# Revit family: Shower-Handshower_Kit-KOHLER-Fore_Arc-K-35732T
name_source: partatom
category: Plumbing Fixtures
units: mm (PartAtom-declared; Revit-internal decimal feet)

## family parameters
Cut with Voids When Loaded = No
Host = Face
Maintain Annotation Orientation = No
OmniClass Number = 23.31.17.00
OmniClass Title = Showers
Part Type = Normal
Room Calculation Point = No
Round Connector Dimension = Use Diameter
Shared = No

## types (4) — shared parameters
ADA Compliant = No
Assembly Code = D2010700
CW Connection = Yes
Cold Water Inlet = Cold Water Inlet
Date Modified = 10/06/2025
Default Elevation = 42"
Description = Exposed Bath Shower Faucet
Drain Included = No
Flow Rate = 0 GPM
HW Connection = Yes
Handle Clearance = 3 9/16"
Height = 19 1/2"
Hot Water Inlet = Hot Water Inlet
Length = 4 3/16"
Manufacturer = Kohler Co.
Master Format 2014 = 22 42 23
Master Format 2014 Name = Residential Showers
Material = Premium Metal Construction
Pressure = 0.00 psi
Product Name = Fore Line
Spout Reach = 6 11/16"
URL = http://www.kohler.com.cn
Vent Connection = No
Waste Connection = No
Waste Water Outlet = Waste Water Outlet
WaterSense Certified = No
Width = 5 7/8"

## per-type parameters (varying)
| type | Finish | Model | Secondary Finish | Type |
| BL-Matte Black | Kohler-Metal-BL-Matte_Black | K-35732T-4-BL | Plastic-Pantone-PQ-194205-TCX | 1 |
| BN-Vibrant Brushed Nickel | Kohler-Metal-BN-Vibrant_Brushed_Nickel | K-35732T-4-BN | Kohler-Plastic-0-White | 2 |
| CP-Polished Chrome | Kohler-Metal-CP-Polished_Chrome | K-35732T-4-CP | Kohler-Plastic-0-White | 3 |
| LBN-Non Pvd Brushed Nickel | Kohler-Metal-LBN-Non_Pvd_Brushed_Nickel | K-35732T-4-LBN | Kohler-Plastic-0-White | 4 |

## geometry (parser evidence)
native form markers: Sweep x10
no freeform markers — native parametric forms only
